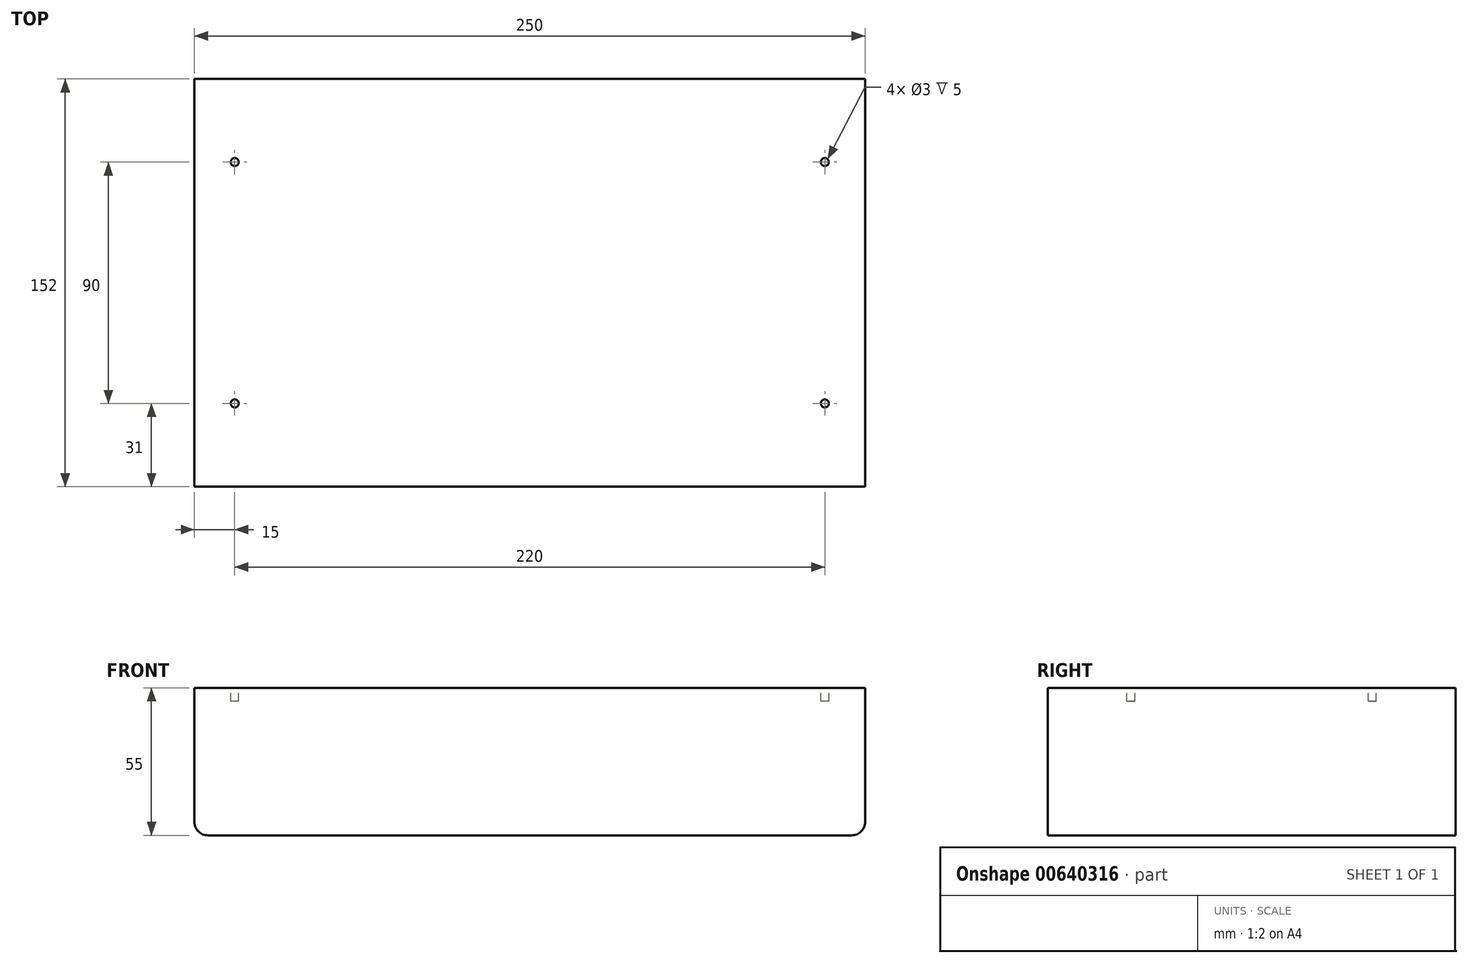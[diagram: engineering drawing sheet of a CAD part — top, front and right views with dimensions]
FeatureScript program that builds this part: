
annotation { "Feature Type Name" : "Feature", "Feature Type Description" : "" }
export const myFeature = defineFeature(function(context is Context, id is Id, definition is map)
    precondition{}
    {
        {
            var Q0;
            Q0=qCreatedBy(makeId("Top.planeOp"),FACE);
            var sketch = newSketch(context, id + "F0", { "sketchPlane" : qUnion([Q0])});
            skLineSegment(sketch, "E0.bottom", {"start": v(125, -76) * mm, "end": v(-125, -76) * mm});
            skLineSegment(sketch, "E0.top", {"start": v(125, 76) * mm, "end": v(-125, 76) * mm});
            skLineSegment(sketch, "E0.left", {"start": v(125, -76) * mm, "end": v(125, 76) * mm});
            skLineSegment(sketch, "E0.right", {"start": v(-125, -76) * mm, "end": v(-125, 76) * mm});
            skPoint(sketch, "E0.middle", {"position": v(0, 0) * mm});
            skSolve(sketch);
        }
        {
            var Q0;
            Q0 = qSketchRegion(id + "F0", true);
            extrude(context, id + "F1", {"entities" : qUnion([Q0]), "depth" : 55 * mm, "offsetDistance" : 25 * mm});
        }
        {
            var Q0;
            Q0=makeQuery(id+"F1.opExtrude","CAP_FACE",FACE,{"disambiguationData":[OSD([sQuery(id+"F0.wireOp",EDGE,"E0.bottom"),sQuery(id+"F0.wireOp",EDGE,"E0.top"),sQuery(id+"F0.wireOp",EDGE,"E0.left"),sQuery(id+"F0.wireOp",EDGE,"E0.right")])],"isStart":false});
            var sketch = newSketch(context, id + "F2", { "sketchPlane" : qUnion([Q0])});
            skLineSegment(sketch, "E1.bottom", {"start": v(110, -45) * mm, "end": v(-110, -45) * mm, "construction": true});
            skLineSegment(sketch, "E1.top", {"start": v(110, 45) * mm, "end": v(-110, 45) * mm, "construction": true});
            skLineSegment(sketch, "E1.left", {"start": v(110, -45) * mm, "end": v(110, 45) * mm, "construction": true});
            skLineSegment(sketch, "E1.right", {"start": v(-110, -45) * mm, "end": v(-110, 45) * mm, "construction": true});
            skPoint(sketch, "E1.middle", {"position": v(0, 0) * mm});
            skCircle(sketch, "E2", {"center": v(-110, 45) * mm, "radius": 1.5 * mm});
            skCircle(sketch, "E3.MirrorC", {"center": v(110, 45) * mm, "radius": 1.5 * mm});
            skCircle(sketch, "E4.MirrorC", {"center": v(-110, -45) * mm, "radius": 1.5 * mm});
            skCircle(sketch, "E5.MirrorC", {"center": v(110, -45) * mm, "radius": 1.5 * mm});
            skSolve(sketch);
        }
        {
            var Q0;
            Q0 = qSketchRegion(id + "F2", true);
            extrude(context, id + "F3", {"entities" : qUnion([Q0]), "operationType" : NewBodyOperationType.REMOVE, "oppositeDirection" : true, "depth" : 5 * mm, "offsetDistance" : 25 * mm});
        }
        {
            var Q0;
            Q0=makeQuery(id+"F1.opExtrude","CAP_EDGE",EDGE,{"disambiguationData":[OSD([sQuery(id+"F0.wireOp",EDGE,"E0.right")])],"isStart":true});
            var Q1;
            Q1=makeQuery(id+"F1.opExtrude","CAP_EDGE",EDGE,{"disambiguationData":[OSD([sQuery(id+"F0.wireOp",EDGE,"E0.left")])],"isStart":true});
            fillet(context, id + "F4", {"entities" : qUnion([Q0, Q1]), "radius" : 5 * mm, "tangentPropagation" : true, "allowEdgeOverflow" : false});
        }
    });
